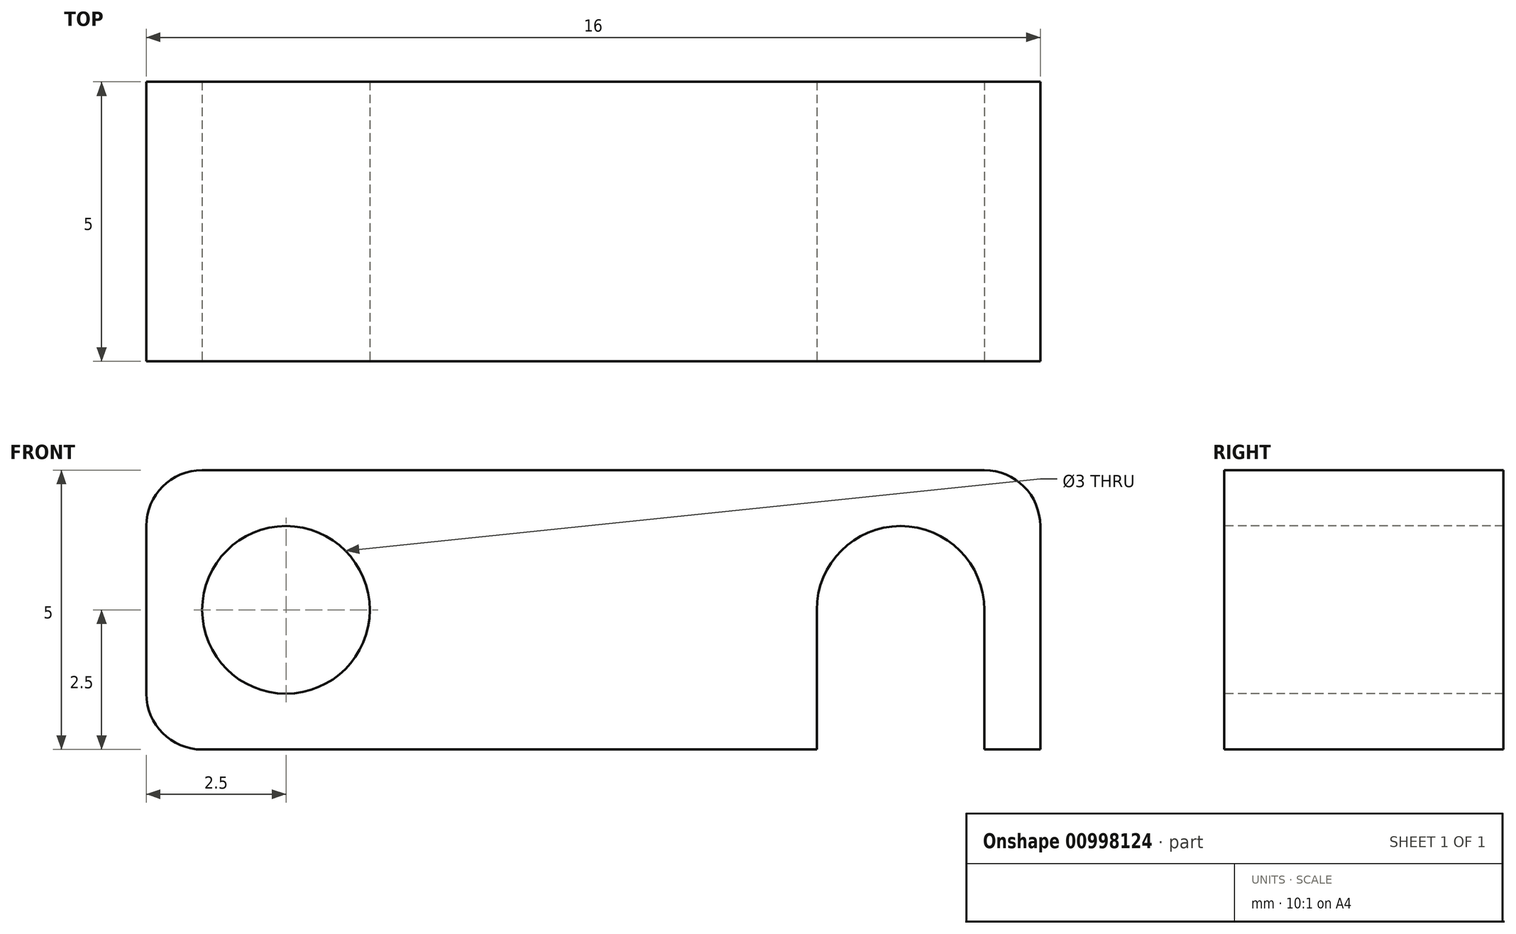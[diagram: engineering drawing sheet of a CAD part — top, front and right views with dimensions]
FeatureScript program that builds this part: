
annotation { "Feature Type Name" : "Feature", "Feature Type Description" : "" }
export const myFeature = defineFeature(function(context is Context, id is Id, definition is map)
    precondition{}
    {
        {
            var Q0;
            Q0=qCreatedBy(makeId("Front.planeOp"),FACE);
            var sketch = newSketch(context, id + "F0", { "sketchPlane" : qUnion([Q0])});
            skLineSegment(sketch, "E0.bottom", {"start": v(0, 0) * mm, "end": v(16, 0) * mm});
            skLineSegment(sketch, "E0.top", {"start": v(0, 5) * mm, "end": v(16, 5) * mm});
            skLineSegment(sketch, "E0.left", {"start": v(0, 0) * mm, "end": v(0, 5) * mm});
            skLineSegment(sketch, "E0.right", {"start": v(16, 0) * mm, "end": v(16, 5) * mm});
            skSolve(sketch);
        }
        {
            var Q0;
            Q0 = qSketchRegion(id + "F0", true);
            extrude(context, id + "F1", {"entities" : qUnion([Q0]), "depth" : 5 * mm, "offsetDistance" : 25 * mm});
        }
        {
            var Q0;
            Q0=makeQuery(id+"F1.opExtrude","CAP_FACE",FACE,{"disambiguationData":[OSD([sQuery(id+"F0.wireOp",EDGE,"E0.bottom"),sQuery(id+"F0.wireOp",EDGE,"E0.top"),sQuery(id+"F0.wireOp",EDGE,"E0.left"),sQuery(id+"F0.wireOp",EDGE,"E0.right")])],"isStart":false});
            var sketch = newSketch(context, id + "F2", { "sketchPlane" : qUnion([Q0])});
            skCircle(sketch, "E1", {"center": v(2.5, 2.5) * mm, "radius": 1.5 * mm});
            skArc(sketch, "E2", {"start": v(15, 2.5) * mm, "mid": v(13.5, 4) * mm, "end": v(12, 2.5) * mm});
            skLineSegment(sketch, "E3", {"start": v(12, 2.5) * mm, "end": v(12, 0) * mm});
            skLineSegment(sketch, "E4", {"start": v(15, 2.5) * mm, "end": v(15, 0) * mm});
            skLineSegment(sketch, "E5", {"start": v(0, 2.5) * mm, "end": v(16, 2.5) * mm, "construction": true});
            skSolve(sketch);
        }
        {
            var Q0;
            Q0=makeQuery(id+"F2.imprint","IMPRINT",FACE,{"disambiguationData":[TD([[makeQuery(id+"F2.imprint","IMPRINT",EDGE,{"derivedFrom":sQuery(id+"F2.wireOp",EDGE,"E1")}),1.0]])]});
            var Q1;
            Q1=makeQuery(id+"F2.imprint","IMPRINT",FACE,{"disambiguationData":[TD([[makeQuery(id+"F2.imprint","IMPRINT",EDGE,{"derivedFrom":sQuery(id+"F2.wireOp",EDGE,"E2")}),1.0]])]});
            extrude(context, id + "F3", {"entities" : qUnion([Q0, Q1]), "operationType" : NewBodyOperationType.REMOVE, "endBound" : BoundingType.THROUGH_ALL, "oppositeDirection" : true, "depth" : 25 * mm, "offsetDistance" : 25 * mm});
        }
        {
            var Q0;
            Q0=makeQuery(id+"F1.opExtrude","SWEPT_EDGE",EDGE,{"disambiguationData":[OSD([sQuery(id+"F0.wireOp",EDGE,"E0.bottom"),sQuery(id+"F0.wireOp",EDGE,"E0.left")])]});
            var Q1;
            Q1=makeQuery(id+"F1.opExtrude","SWEPT_EDGE",EDGE,{"disambiguationData":[OSD([sQuery(id+"F0.wireOp",EDGE,"E0.top"),sQuery(id+"F0.wireOp",EDGE,"E0.left")])]});
            var Q2;
            Q2=makeQuery(id+"F1.opExtrude","SWEPT_EDGE",EDGE,{"disambiguationData":[OSD([sQuery(id+"F0.wireOp",EDGE,"E0.top"),sQuery(id+"F0.wireOp",EDGE,"E0.right")])]});
            fillet(context, id + "F4", {"entities" : qUnion([Q0, Q1, Q2]), "radius" : 1 * mm, "tangentPropagation" : true, "allowEdgeOverflow" : false});
        }
    });
